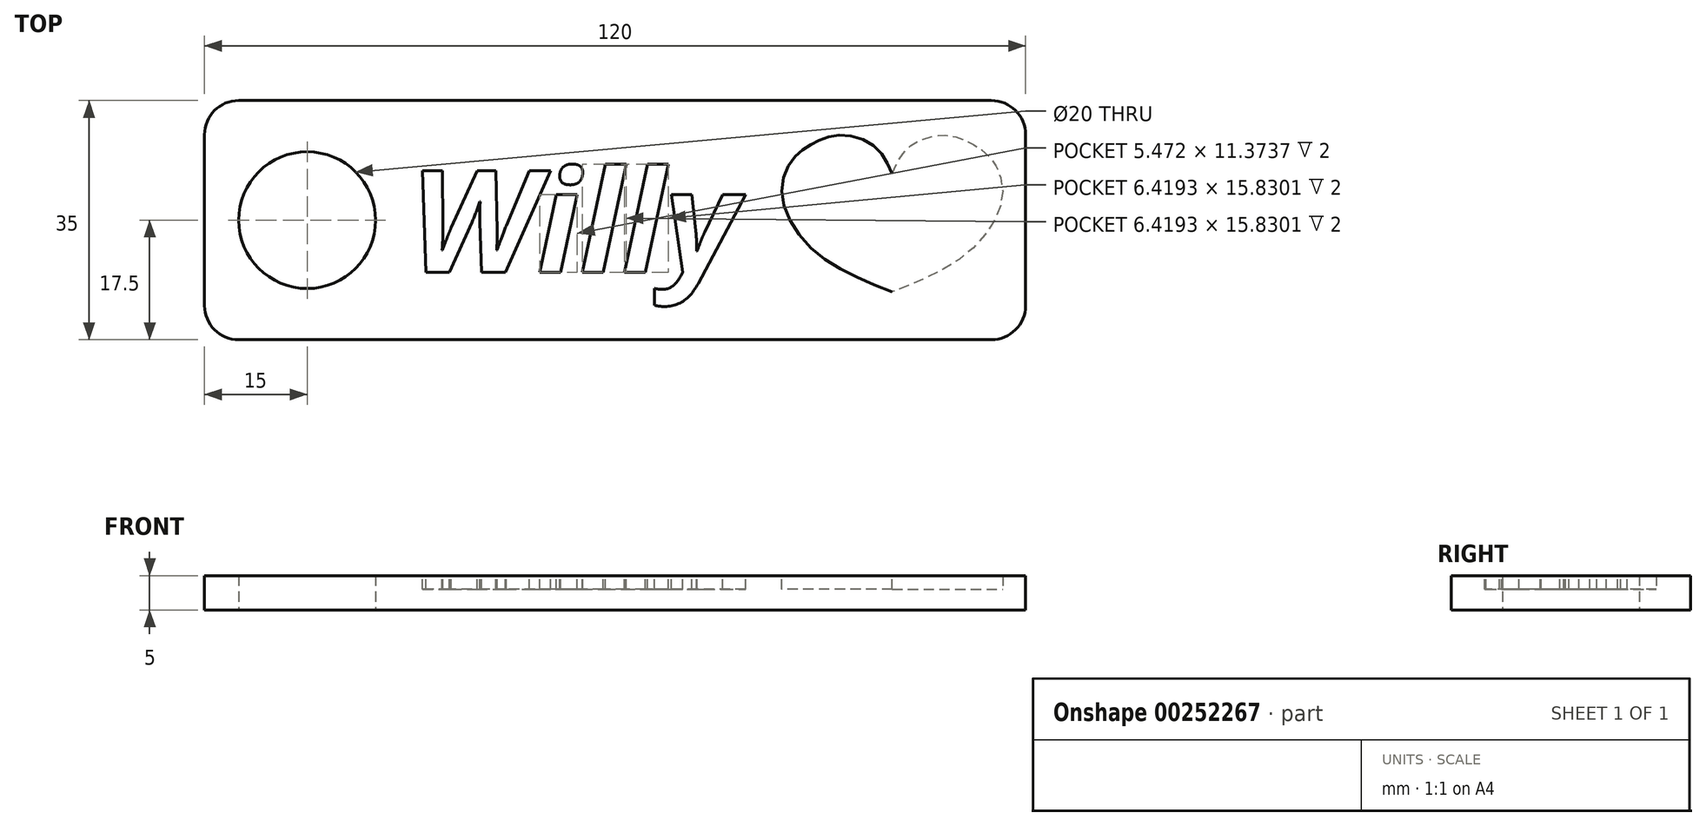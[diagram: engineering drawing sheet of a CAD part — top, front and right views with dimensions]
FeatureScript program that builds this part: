
annotation { "Feature Type Name" : "Feature", "Feature Type Description" : "" }
export const myFeature = defineFeature(function(context is Context, id is Id, definition is map)
    precondition{}
    {
        {
            var Q0;
            Q0=qCreatedBy(makeId("Top.planeOp"),FACE);
            var sketch = newSketch(context, id + "F0", { "sketchPlane" : qUnion([Q0])});
            skLineSegment(sketch, "E0.bottom", {"start": v(60, 17.5) * mm, "end": v(-60, 17.5) * mm});
            skLineSegment(sketch, "E0.top", {"start": v(60, -17.5) * mm, "end": v(-60, -17.5) * mm});
            skLineSegment(sketch, "E0.left", {"start": v(60, 17.5) * mm, "end": v(60, -17.5) * mm});
            skLineSegment(sketch, "E0.right", {"start": v(-60, 17.5) * mm, "end": v(-60, -17.5) * mm});
            skPoint(sketch, "E0.middle", {"position": v(0, 0) * mm});
            skCircle(sketch, "E1", {"center": v(-45, 0) * mm, "radius": 10 * mm});
            skSolve(sketch);
        }
        {
            var Q0;
            Q0=makeQuery(id+"F0.imprint","IMPRINT",FACE,{"disambiguationData":[TD([[makeQuery(id+"F0.imprint","IMPRINT",EDGE,{"derivedFrom":sQuery(id+"F0.wireOp",EDGE,"E0.bottom")}),1.0]])]});
            extrude(context, id + "F1", {"entities" : qUnion([Q0]), "depth" : 5 * mm});
        }
        {
            var Q0;
            Q0=makeQuery(id+"F1.opExtrude","SWEPT_EDGE",EDGE,{"disambiguationData":[OSD([sQuery(id+"F0.wireOp",EDGE,"E0.top"),sQuery(id+"F0.wireOp",EDGE,"E0.left")])]});
            var Q1;
            Q1=makeQuery(id+"F1.opExtrude","SWEPT_EDGE",EDGE,{"disambiguationData":[OSD([sQuery(id+"F0.wireOp",EDGE,"E0.top"),sQuery(id+"F0.wireOp",EDGE,"E0.right")])]});
            var Q2;
            Q2=makeQuery(id+"F1.opExtrude","SWEPT_EDGE",EDGE,{"disambiguationData":[OSD([sQuery(id+"F0.wireOp",EDGE,"E0.bottom"),sQuery(id+"F0.wireOp",EDGE,"E0.left")])]});
            var Q3;
            Q3=makeQuery(id+"F1.opExtrude","SWEPT_EDGE",EDGE,{"disambiguationData":[OSD([sQuery(id+"F0.wireOp",EDGE,"E0.bottom"),sQuery(id+"F0.wireOp",EDGE,"E0.right")])]});
            fillet(context, id + "F2", {"entities" : qUnion([Q0, Q1, Q2, Q3]), "radius" : 5 * mm, "tangentPropagation" : true, "allowEdgeOverflow" : false});
        }
        {
            var Q0;
            Q0 = qSketchRegion(id + "F0", true);
            extrude(context, id + "F3", {"entities" : qUnion([Q0]), "operationType" : NewBodyOperationType.ADD, "depth" : 5 * mm});
        }
        {
            var Q0;
            Q0=makeQuery(id+"F3.opExtrude","SWEPT_EDGE",EDGE,{"disambiguationData":[OSD([sQuery(id+"F0.wireOp",EDGE,"E0.bottom"),sQuery(id+"F0.wireOp",EDGE,"E0.right")])]});
            var Q1;
            Q1=makeQuery(id+"F3.opExtrude","SWEPT_EDGE",EDGE,{"disambiguationData":[OSD([sQuery(id+"F0.wireOp",EDGE,"E0.bottom"),sQuery(id+"F0.wireOp",EDGE,"E0.left")])]});
            var Q2;
            Q2=makeQuery(id+"F3.opExtrude","SWEPT_EDGE",EDGE,{"disambiguationData":[OSD([sQuery(id+"F0.wireOp",EDGE,"E0.top"),sQuery(id+"F0.wireOp",EDGE,"E0.right")])]});
            var Q3;
            Q3=makeQuery(id+"F3.opExtrude","SWEPT_EDGE",EDGE,{"disambiguationData":[OSD([sQuery(id+"F0.wireOp",EDGE,"E0.top"),sQuery(id+"F0.wireOp",EDGE,"E0.left")])]});
            fillet(context, id + "F4", {"entities" : qUnion([Q0, Q1, Q2, Q3]), "radius" : 5 * mm, "tangentPropagation" : true, "allowEdgeOverflow" : false});
        }
        {
            var Q0;
            {var subQ0=sQuery(id+"F0.wireOp",EDGE,"E1");var subQ1=sQuery(id+"F0.wireOp",EDGE,"E0.right");var subQ2=sQuery(id+"F0.wireOp",EDGE,"E0.left");var subQ3=sQuery(id+"F0.wireOp",EDGE,"E0.top");var subQ4=sQuery(id+"F0.wireOp",EDGE,"E0.bottom");Q0=makeQuery(id+"F3.boolean.opBoolean","MERGE",FACE,{"derivedFrom":[makeQuery(id+"F1.opExtrude","CAP_FACE",FACE,{"disambiguationData":[OSD([subQ4,subQ3,subQ2,subQ1,subQ0])],"isStart":false}),makeQuery(id+"F3.opExtrude","CAP_FACE",FACE,{"disambiguationData":[OSD([subQ4,subQ3,subQ2,subQ1,subQ0])],"isStart":false})]});}
            var sketch = newSketch(context, id + "F5", { "sketchPlane" : qUnion([Q0])});
            skText(sketch, "E2", { "text": "Willy", "fontName": "OpenSans-BoldItalic.ttf"});
            skLineSegment(sketch, "E3", {"start": v(40.5, 53.54) * mm, "end": v(40.5, -47.3) * mm, "construction": true});
            skFitSpline(sketch, "E4", {"points": [v(40.5, 6.8) * mm, v(37.96, 10.76) * mm, v(32.86, 12.46) * mm, v(29.18, 11.33) * mm, v(26.34, 9.35) * mm, v(24.36, 3.97) * mm, v(29.18, -4.53) * mm, v(40.5, -10.48) * mm], "startDerivative": vector(-15.46, 35.14) * mm, "endDerivative": vector(59.98, -23.46) * mm});
            skFitSpline(sketch, "E5.MirrorCS", {"points": [v(40.5, 6.8) * mm, v(43.06, 10.76) * mm, v(48.16, 12.46) * mm, v(51.84, 11.33) * mm, v(54.67, 9.35) * mm, v(56.65, 3.97) * mm, v(51.84, -4.53) * mm, v(40.5, -10.48) * mm], "startDerivative": vector(15.46, 35.14) * mm, "endDerivative": vector(-59.98, -23.46) * mm});
            const initialGuessF5  = {"E2": [-0.02999, -0.00762, 1, 0, 0.015]};
            skSetInitialGuess(sketch, initialGuessF5);
            skSolve(sketch);
        }
        {
            var Q0;
            Q0 = qSketchRegion(id + "F5", true);
            extrude(context, id + "F6", {"entities" : qUnion([Q0]), "operationType" : NewBodyOperationType.REMOVE, "oppositeDirection" : true, "depth" : 2 * mm});
        }
    });
